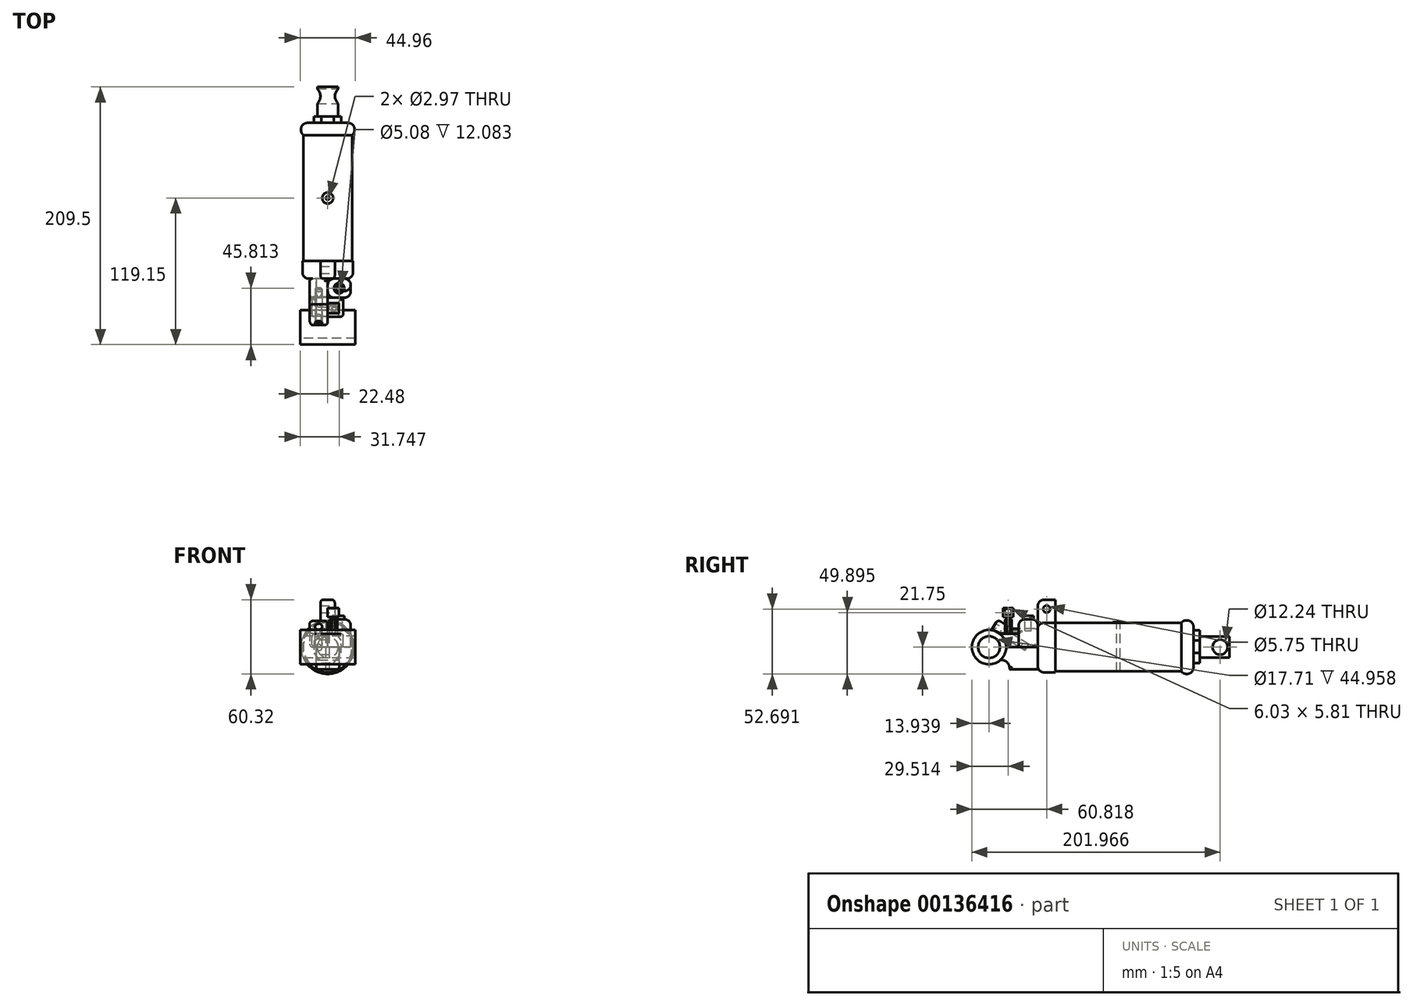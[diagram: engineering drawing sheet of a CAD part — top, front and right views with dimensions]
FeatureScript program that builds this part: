
annotation { "Feature Type Name" : "Feature", "Feature Type Description" : "" }
export const myFeature = defineFeature(function(context is Context, id is Id, definition is map)
    precondition{}
    {
        {
            var Q0;
            Q0=qCreatedBy(makeId("Front.planeOp"),FACE);
            var sketch = newSketch(context, id + "F0", { "sketchPlane" : qUnion([Q0])});
            skCircle(sketch, "E0", {"center": v(0, 0) * mm, "radius": 19.78 * mm});
            skSolve(sketch);
        }
        {
            var Q0;
            Q0=qSketchRegion(id+"F0",true);
            extrude(context, id + "F1", {"entities" : qUnion([Q0]), "endBound" : BoundingType.SYMMETRIC, "depth" : 102.44 * mm});
        }
        {
            var Q0;
            Q0=makeQuery(id+"F1.opExtrude","CAP_FACE",FACE,{"disambiguationData":[OSD([sQuery(id+"F0.wireOp",EDGE,"E0")])],"isStart":true});
            var sketch = newSketch(context, id + "F2", { "sketchPlane" : qUnion([Q0])});
            skCircle(sketch, "E1", {"center": v(0, 0) * mm, "radius": 21.75 * mm});
            skSolve(sketch);
        }
        {
            var Q0;
            Q0=qSketchRegion(id+"F2",true);
            extrude(context, id + "F3", {"entities" : qUnion([Q0]), "operationType" : NewBodyOperationType.ADD, "depth" : 9.88 * mm});
        }
        {
            var Q0;
            Q0=makeQuery(id+"F3.opExtrude","CAP_FACE",FACE,{"disambiguationData":[OSD([sQuery(id+"F2.wireOp",EDGE,"E1")])],"isStart":false});
            var sketch = newSketch(context, id + "F4", { "sketchPlane" : qUnion([Q0])});
            skLineSegment(sketch, "E2", {"start": v(-4.97, 13.58) * mm, "end": v(5.19, 13.58) * mm});
            skLineSegment(sketch, "E3", {"start": v(5.19, 13.58) * mm, "end": v(11.28, 5.45) * mm});
            skLineSegment(sketch, "E4", {"start": v(11.28, 5.45) * mm, "end": v(11.28, -4.7) * mm});
            skLineSegment(sketch, "E5", {"start": v(11.28, -4.7) * mm, "end": v(5.19, -12.84) * mm});
            skLineSegment(sketch, "E6", {"start": v(5.19, -12.84) * mm, "end": v(-4.97, -12.84) * mm});
            skLineSegment(sketch, "E7", {"start": v(-4.97, -12.84) * mm, "end": v(-11.07, -4.7) * mm});
            skLineSegment(sketch, "E8", {"start": v(-11.07, -4.7) * mm, "end": v(-11.07, 5.45) * mm});
            skLineSegment(sketch, "E9", {"start": v(-11.07, 5.45) * mm, "end": v(-4.97, 13.58) * mm});
            skSolve(sketch);
        }
        {
            var Q0;
            Q0=qSketchRegion(id+"F4",true);
            extrude(context, id + "F5", {"entities" : qUnion([Q0]), "operationType" : NewBodyOperationType.ADD, "depth" : 5.07 * mm});
        }
        {
            var Q0;
            Q0=makeQuery(id+"F5.opExtrude","CAP_FACE",FACE,{"disambiguationData":[OSD([sQuery(id+"F4.wireOp",EDGE,"E2"),sQuery(id+"F4.wireOp",EDGE,"E3"),sQuery(id+"F4.wireOp",EDGE,"E4"),sQuery(id+"F4.wireOp",EDGE,"E5"),sQuery(id+"F4.wireOp",EDGE,"E6"),sQuery(id+"F4.wireOp",EDGE,"E7"),sQuery(id+"F4.wireOp",EDGE,"E8"),sQuery(id+"F4.wireOp",EDGE,"E9")])],"isStart":false});
            var sketch = newSketch(context, id + "F6", { "sketchPlane" : qUnion([Q0])});
            skCircle(sketch, "E10", {"center": v(0, 0) * mm, "radius": 8.5 * mm});
            skSolve(sketch);
        }
        {
            var Q0;
            Q0=qSketchRegion(id+"F6",true);
            extrude(context, id + "F7", {"entities" : qUnion([Q0]), "operationType" : NewBodyOperationType.ADD, "depth" : 24.18 * mm});
        }
        {
            var Q0;
            Q0=qCreatedBy(makeId("Right.planeOp"),FACE);
            var sketch = newSketch(context, id + "F8", { "sketchPlane" : qUnion([Q0])});
            skCircle(sketch, "E11", {"center": v(82.82, 0) * mm, "radius": 6.12 * mm});
            skSolve(sketch);
        }
        {
            var Q0;
            Q0=qSketchRegion(id+"F8",true);
            extrude(context, id + "F9", {"entities" : qUnion([Q0]), "operationType" : NewBodyOperationType.REMOVE, "endBound" : BoundingType.SYMMETRIC, "oppositeDirection" : true, "depth" : 25.4 * mm});
        }
        {
            var Q0;
            Q0=qCreatedBy(makeId("Top.planeOp"),FACE);
            cPlane(context, id + "F10", {"entities" : qUnion([Q0]), "cplaneType" : CPlaneType.OFFSET, "offset" : 19.78 * mm, "width" : 152.4 * mm, "height" : 152.4 * mm});
        }
        {
            var Q0;
            Q0=qCreatedBy(id+"F10.planeOp",FACE);
            var sketch = newSketch(context, id + "F11", { "sketchPlane" : qUnion([Q0])});
            skCircle(sketch, "E12", {"center": v(0, 0) * mm, "radius": 4.5 * mm});
            skSolve(sketch);
        }
        {
            var Q0;
            Q0=qSketchRegion(id+"F11",true);
            extrude(context, id + "F12", {"entities" : qUnion([Q0]), "depth" : 0.62 * mm});
        }
        {
            var Q0;
            Q0=makeQuery(id+"F12.opExtrude","CAP_FACE",FACE,{"disambiguationData":[OSD([sQuery(id+"F11.wireOp",EDGE,"E12")])],"isStart":false});
            var sketch = newSketch(context, id + "F13", { "sketchPlane" : qUnion([Q0])});
            skCircle(sketch, "E13", {"center": v(0, 0) * mm, "radius": 1.48 * mm});
            skSolve(sketch);
        }
        {
            var Q0;
            Q0=qSketchRegion(id+"F13",true);
            extrude(context, id + "F14", {"entities" : qUnion([Q0]), "operationType" : NewBodyOperationType.REMOVE, "oppositeDirection" : true, "depth" : 152.4 * mm});
        }
        {
            var Q0;
            Q0=makeQuery(id+"F1.opExtrude","CAP_FACE",FACE,{"disambiguationData":[OSD([sQuery(id+"F0.wireOp",EDGE,"E0")])],"isStart":false});
            var sketch = newSketch(context, id + "F15", { "sketchPlane" : qUnion([Q0])});
            skCircle(sketch, "E14", {"center": v(0, 0) * mm, "radius": 20.57 * mm});
            skLineSegment(sketch, "E15", {"start": v(-5.98, 19.68) * mm, "end": v(-5.98, 38.57) * mm});
            skLineSegment(sketch, "E16", {"start": v(-5.98, 38.57) * mm, "end": v(5.75, 38.57) * mm});
            skLineSegment(sketch, "E17", {"start": v(5.75, 38.57) * mm, "end": v(5.75, 19.75) * mm});
            skSolve(sketch);
        }
        {
            var Q0;
            Q0=qSketchRegion(id+"F15",true);
            extrude(context, id + "F16", {"entities" : qUnion([Q0]), "operationType" : NewBodyOperationType.ADD, "depth" : 14.33 * mm});
        }
        {
            var Q0;
            Q0=makeQuery(id+"F16.opExtrude","CAP_EDGE",EDGE,{"disambiguationData":[OSD([sQuery(id+"F15.wireOp",EDGE,"E16")])],"isStart":false});
            fillet(context, id + "F17", {"entities" : qUnion([Q0]), "radius" : 5.08 * mm, "tangentPropagation" : true, "allowEdgeOverflow" : false});
        }
        {
            var Q0;
            Q0=makeQuery(id+"F16.opExtrude","SWEPT_EDGE",EDGE,{"disambiguationData":[OSD([sQuery(id+"F15.wireOp",EDGE,"E16"),sQuery(id+"F15.wireOp",EDGE,"E17")])]});
            var Q1;
            Q1=makeQuery(id+"F16.opExtrude","SWEPT_EDGE",EDGE,{"disambiguationData":[OSD([sQuery(id+"F15.wireOp",EDGE,"E15"),sQuery(id+"F15.wireOp",EDGE,"E16")])]});
            fillet(context, id + "F18", {"entities" : qUnion([Q0, Q1]), "radius" : 2.54 * mm, "tangentPropagation" : true, "allowEdgeOverflow" : false});
        }
        {
            var Q0;
            Q0=makeQuery(id+"F16.opExtrude","SWEPT_FACE",FACE,{"disambiguationData":[OSD([sQuery(id+"F15.wireOp",EDGE,"E17")])]});
            var sketch = newSketch(context, id + "F19", { "sketchPlane" : qUnion([Q0])});
            skCircle(sketch, "E18", {"center": v(-58.33, 30.94) * mm, "radius": 2.87 * mm});
            skSolve(sketch);
        }
        {
            var Q0;
            Q0=qSketchRegion(id+"F19",true);
            extrude(context, id + "F20", {"entities" : qUnion([Q0]), "operationType" : NewBodyOperationType.REMOVE, "endBound" : BoundingType.THROUGH_ALL, "oppositeDirection" : true, "depth" : 25.4 * mm});
        }
        {
            var Q0;
            Q0=qCreatedBy(makeId("Right.planeOp"),FACE);
            var sketch = newSketch(context, id + "F21", { "sketchPlane" : qUnion([Q0])});
            skLineSegment(sketch, "E19", {"start": v(-65.55, -17.99) * mm, "end": v(-88.58, -17.99) * mm});
            skArc(sketch, "E20", {"start": v(-88.58, -17.99) * mm, "mid": v(-90.47, -12.4) * mm, "end": v(-96.05, -10.5) * mm});
            skCircle(sketch, "E21", {"center": v(-105.21, 0) * mm, "radius": 13.94 * mm});
            skCircle(sketch, "E22", {"center": v(-105.21, 0) * mm, "radius": 8.86 * mm});
            skLineSegment(sketch, "E23", {"start": v(-96.43, 10.84) * mm, "end": v(-81.06, 10.84) * mm});
            skLineSegment(sketch, "E24", {"start": v(-81.06, 0) * mm, "end": v(-81.06, 22.72) * mm});
            skLineSegment(sketch, "E25", {"start": v(-81.06, 22.72) * mm, "end": v(-65.54, 22.72) * mm});
            skLineSegment(sketch, "E26", {"start": v(-65.54, 22.72) * mm, "end": v(-65.55, -17.99) * mm});
            skLineSegment(sketch, "E27", {"start": v(-81.06, 0) * mm, "end": v(-65.54, 0) * mm});
            skLineSegment(sketch, "E28", {"start": v(-81.06, 0) * mm, "end": v(-91.27, 0) * mm});
            skSolve(sketch);
        }
        {
            var Q0;
            {var subQ1=sQuery(id+"F21.wireOp",EDGE,"E19");Q0=makeQuery(id+"F21.imprint","IMPRINT",FACE,{"disambiguationData":[TD([[makeQuery(id+"F21.imprint","IMPRINT",EDGE,{"derivedFrom":subQ1}),-1.0]])]});}
            extrude(context, id + "F22", {"entities" : qUnion([Q0]), "endBound" : BoundingType.SYMMETRIC, "oppositeDirection" : true, "depth" : 18.93 * mm});
        }
        {
            var Q0;
            {var subQ0=sQuery(id+"F21.wireOp",EDGE,"E25");Q0=makeQuery(id+"F21.imprint","IMPRINT",FACE,{"disambiguationData":[TD([[makeQuery(id+"F21.imprint","IMPRINT",EDGE,{"derivedFrom":subQ0}),-1.0]])]});}
            extrude(context, id + "F23", {"entities" : qUnion([Q0]), "depth" : 18.67 * mm});
        }
        {
            var Q0;
            {var subQ0=sQuery(id+"F21.wireOp",EDGE,"E23");Q0=makeQuery(id+"F21.imprint","IMPRINT",FACE,{"disambiguationData":[TD([[makeQuery(id+"F21.imprint","IMPRINT",EDGE,{"derivedFrom":subQ0}),-1.0]])]});}
            extrude(context, id + "F24", {"entities" : qUnion([Q0]), "endBound" : BoundingType.SYMMETRIC, "depth" : 25.4 * mm});
        }
        {
            var Q0;
            Q0=makeQuery(id+"F21.imprint","IMPRINT",FACE,{"disambiguationData":[TD([[makeQuery(id+"F21.imprint","IMPRINT",EDGE,{"derivedFrom":sQuery(id+"F21.wireOp",EDGE,"E22")}),-1.0]])]});
            extrude(context, id + "F25", {"entities" : qUnion([Q0]), "endBound" : BoundingType.SYMMETRIC, "depth" : 44.96 * mm});
        }
        {
            var Q0;
            Q0=makeQuery(id+"F23.opExtrude","CAP_EDGE",EDGE,{"disambiguationData":[OSD([sQuery(id+"F21.wireOp",EDGE,"E25")])],"isStart":false});
            var Q1;
            Q1=makeQuery(id+"F23.opExtrude","CAP_EDGE",EDGE,{"disambiguationData":[OSD([sQuery(id+"F21.wireOp",EDGE,"E24")])],"isStart":false});
            var Q2;
            Q2=makeQuery(id+"F23.opExtrude","CAP_EDGE",EDGE,{"disambiguationData":[OSD([sQuery(id+"F21.wireOp",EDGE,"E26")])],"isStart":false});
            var Q3;
            Q3=makeQuery(id+"F23.opExtrude","SWEPT_EDGE",EDGE,{"disambiguationData":[OSD([sQuery(id+"F21.wireOp",EDGE,"E25"),sQuery(id+"F21.wireOp",EDGE,"E26")])]});
            var Q4;
            Q4=makeQuery(id+"F23.opExtrude","CAP_EDGE",EDGE,{"disambiguationData":[OSD([sQuery(id+"F21.wireOp",EDGE,"E24")])],"isStart":true});
            var Q5;
            Q5=makeQuery(id+"F23.opExtrude","CAP_EDGE",EDGE,{"disambiguationData":[OSD([sQuery(id+"F21.wireOp",EDGE,"E25")])],"isStart":true});
            fillet(context, id + "F26", {"entities" : qUnion([Q0, Q1, Q2, Q3, Q4, Q5]), "radius" : 5.08 * mm, "tangentPropagation" : true, "allowEdgeOverflow" : false});
        }
        {
            var Q0;
            Q0=makeQuery(id+"F16.opExtrude","CAP_EDGE",EDGE,{"disambiguationData":[OSD([sQuery(id+"F15.wireOp",EDGE,"E14")])],"isStart":false});
            var Q1;
            {var subQ0=sQuery(id+"F21.wireOp",EDGE,"E26");var subQ1=sQuery(id+"F21.wireOp",EDGE,"E25");Q1=makeQuery(id+"F26.opFillet","BLEND_FACE",FACE,{"disambiguationData":[OSD([subQ1,subQ0]),TDD([makeQuery(id+"F23.opExtrude","SWEPT_EDGE",EDGE,{"disambiguationData":[OSD([subQ1,subQ0])]})])]});}
            var Q2;
            Q2=makeQuery(id+"F23.opExtrude","SWEPT_EDGE",EDGE,{"disambiguationData":[OSD([sQuery(id+"F21.wireOp",EDGE,"E24"),sQuery(id+"F21.wireOp",EDGE,"E25")])]});
            fillet(context, id + "F27", {"entities" : qUnion([Q0, Q1, Q2]), "radius" : 5.08 * mm, "tangentPropagation" : true, "allowEdgeOverflow" : false});
        }
        {
            var Q0;
            Q0=makeQuery(id+"F23.opExtrude","SWEPT_FACE",FACE,{"disambiguationData":[OSD([sQuery(id+"F21.wireOp",EDGE,"E25")])]});
            var sketch = newSketch(context, id + "F28", { "sketchPlane" : qUnion([Q0])});
            skPoint(sketch, "E29.centerSnap0", {"position": v(9.34, -75.98) * mm});
            skCircle(sketch, "E30", {"center": v(9.27, -73.34) * mm, "radius": 4.22 * mm});
            skSolve(sketch);
        }
        {
            var Q0;
            Q0=qSketchRegion(id+"F28",true);
            extrude(context, id + "F29", {"entities" : qUnion([Q0]), "operationType" : NewBodyOperationType.ADD, "depth" : 2.35 * mm});
        }
        {
            var Q0;
            Q0=qSketchRegion(id+"F28",true);
            extrude(context, id + "F30", {"entities" : qUnion([Q0]), "operationType" : NewBodyOperationType.ADD, "depth" : 2.86 * mm});
        }
        {
            var Q0;
            Q0=makeQuery(id+"F30.opExtrude","CAP_FACE",FACE,{"disambiguationData":[OSD([sQuery(id+"F28.wireOp",EDGE,"E30")])],"isStart":false});
            var sketch = newSketch(context, id + "F31", { "sketchPlane" : qUnion([Q0])});
            skCircle(sketch, "E31", {"center": v(9.27, -73.34) * mm, "radius": 2.54 * mm});
            skSolve(sketch);
        }
        {
            var Q0;
            Q0=qSketchRegion(id+"F31",true);
            extrude(context, id + "F32", {"entities" : qUnion([Q0]), "operationType" : NewBodyOperationType.REMOVE, "oppositeDirection" : true, "depth" : 12.08 * mm});
        }
        {
            var Q0;
            Q0=makeQuery(id+"F24.opExtrude","CAP_EDGE",EDGE,{"disambiguationData":[OSD([sQuery(id+"F21.wireOp",EDGE,"E23")])],"isStart":false});
            var Q1;
            Q1=makeQuery(id+"F24.opExtrude","CAP_EDGE",EDGE,{"disambiguationData":[OSD([sQuery(id+"F21.wireOp",EDGE,"E23")])],"isStart":true});
            var Q2;
            Q2=makeQuery(id+"F24.opExtrude","SWEPT_EDGE",EDGE,{"disambiguationData":[OSD([sQuery(id+"F21.wireOp",EDGE,"E23"),sQuery(id+"F21.wireOp",EDGE,"E24")])]});
            var Q3;
            Q3=makeQuery(id+"F22.opExtrude","CAP_EDGE",EDGE,{"disambiguationData":[OSD([sQuery(id+"F21.wireOp",EDGE,"E27"),sQuery(id+"F21.wireOp",EDGE,"E28")])],"isStart":false});
            var Q4;
            Q4=makeQuery(id+"F22.opExtrude","CAP_EDGE",EDGE,{"disambiguationData":[OSD([sQuery(id+"F21.wireOp",EDGE,"E19")])],"isStart":true});
            var Q5;
            Q5=makeQuery(id+"F22.opExtrude","CAP_EDGE",EDGE,{"disambiguationData":[OSD([sQuery(id+"F21.wireOp",EDGE,"E20")])],"isStart":true});
            var Q6;
            Q6=makeQuery(id+"F24.opExtrude","CAP_EDGE",EDGE,{"disambiguationData":[OSD([sQuery(id+"F21.wireOp",EDGE,"E28")])],"isStart":false});
            fillet(context, id + "F33", {"entities" : qUnion([Q0, Q1, Q2, Q3, Q4, Q5, Q6]), "radius" : 2.03 * mm, "tangentPropagation" : true, "allowEdgeOverflow" : false});
        }
        {
            var Q0;
            Q0=makeQuery(id+"F22.opExtrude","CAP_EDGE",EDGE,{"disambiguationData":[OSD([sQuery(id+"F21.wireOp",EDGE,"E19")])],"isStart":false});
            var Q1;
            Q1=makeQuery(id+"F22.opExtrude","CAP_EDGE",EDGE,{"disambiguationData":[OSD([sQuery(id+"F21.wireOp",EDGE,"E20")])],"isStart":false});
            var Q2;
            Q2=makeQuery(id+"F24.opExtrude","CAP_EDGE",EDGE,{"disambiguationData":[OSD([sQuery(id+"F21.wireOp",EDGE,"E28")])],"isStart":true});
            fillet(context, id + "F34", {"entities" : qUnion([Q0, Q1, Q2]), "radius" : 2.03 * mm, "tangentPropagation" : true, "allowEdgeOverflow" : false});
        }
        {
            var Q0;
            {var subQ0=sQuery(id+"F21.wireOp",EDGE,"E25");Q0=makeQuery(id+"F21.imprint","IMPRINT",FACE,{"disambiguationData":[TD([[makeQuery(id+"F21.imprint","IMPRINT",EDGE,{"derivedFrom":subQ0}),-1.0]])]});}
            var sketch = newSketch(context, id + "F35", { "sketchPlane" : qUnion([Q0])});
            skLineSegment(sketch, "E32", {"start": v(-65.36, 14.9) * mm, "end": v(-86.46, 14.9) * mm});
            skLineSegment(sketch, "E33", {"start": v(-86.46, 14.9) * mm, "end": v(-98.1, 22.23) * mm});
            skLineSegment(sketch, "E34", {"start": v(-98.1, 22.23) * mm, "end": v(-103.37, 13.85) * mm});
            skArc(sketch, "E35", {"start": v(-91.2, 0) * mm, "mid": v(-94.44, 9.43) * mm, "end": v(-103.37, 13.85) * mm});
            skLineSegment(sketch, "E36", {"start": v(-65.36, 14.9) * mm, "end": v(-65.36, 0) * mm});
            skLineSegment(sketch, "E37", {"start": v(-65.36, 0) * mm, "end": v(-80.43, 0) * mm});
            skLineSegment(sketch, "E38", {"start": v(-80.43, 0) * mm, "end": v(-80.43, 11.03) * mm});
            skLineSegment(sketch, "E39", {"start": v(-80.43, 11.03) * mm, "end": v(-96.13, 11.03) * mm});
            skSolve(sketch);
        }
        {
            var Q0;
            Q0=qSketchRegion(id+"F35",true);
            extrude(context, id + "F36", {"entities" : qUnion([Q0]), "oppositeDirection" : true, "depth" : 14.7 * mm});
        }
        {
            var Q0;
            Q0=makeQuery(id+"F36.opExtrude","CAP_EDGE",EDGE,{"disambiguationData":[OSD([sQuery(id+"F35.wireOp",EDGE,"E37")])],"isStart":false});
            var Q1;
            Q1=makeQuery(id+"F36.opExtrude","CAP_EDGE",EDGE,{"disambiguationData":[OSD([sQuery(id+"F35.wireOp",EDGE,"E38")])],"isStart":false});
            var Q2;
            Q2=makeQuery(id+"F36.opExtrude","CAP_EDGE",EDGE,{"disambiguationData":[OSD([sQuery(id+"F35.wireOp",EDGE,"E39")])],"isStart":false});
            var Q3;
            Q3=makeQuery(id+"F36.opExtrude","CAP_EDGE",EDGE,{"disambiguationData":[OSD([sQuery(id+"F35.wireOp",EDGE,"E35")])],"isStart":false});
            var Q4;
            Q4=makeQuery(id+"F36.opExtrude","CAP_EDGE",EDGE,{"disambiguationData":[OSD([sQuery(id+"F35.wireOp",EDGE,"E34")])],"isStart":false});
            var Q5;
            Q5=makeQuery(id+"F36.opExtrude","CAP_EDGE",EDGE,{"disambiguationData":[OSD([sQuery(id+"F35.wireOp",EDGE,"E33")])],"isStart":false});
            var Q6;
            Q6=makeQuery(id+"F36.opExtrude","SWEPT_EDGE",EDGE,{"disambiguationData":[OSD([sQuery(id+"F35.wireOp",EDGE,"E33"),sQuery(id+"F35.wireOp",EDGE,"E34")])]});
            var Q7;
            Q7=makeQuery(id+"F36.opExtrude","CAP_EDGE",EDGE,{"disambiguationData":[OSD([sQuery(id+"F35.wireOp",EDGE,"E32")])],"isStart":false});
            var Q8;
            Q8=makeQuery(id+"F36.opExtrude","CAP_EDGE",EDGE,{"disambiguationData":[OSD([sQuery(id+"F35.wireOp",EDGE,"E32")])],"isStart":true});
            var Q9;
            Q9=makeQuery(id+"F36.opExtrude","SWEPT_EDGE",EDGE,{"disambiguationData":[OSD([sQuery(id+"F35.wireOp",EDGE,"E32"),sQuery(id+"F35.wireOp",EDGE,"E36")])]});
            var Q10;
            Q10=makeQuery(id+"F36.opExtrude","CAP_EDGE",EDGE,{"disambiguationData":[OSD([sQuery(id+"F35.wireOp",EDGE,"E36")])],"isStart":false});
            var Q11;
            Q11=makeQuery(id+"F36.opExtrude","CAP_EDGE",EDGE,{"disambiguationData":[OSD([sQuery(id+"F35.wireOp",EDGE,"E34")])],"isStart":true});
            var Q12;
            Q12=makeQuery(id+"F36.opExtrude","CAP_EDGE",EDGE,{"disambiguationData":[OSD([sQuery(id+"F35.wireOp",EDGE,"E33")])],"isStart":true});
            fillet(context, id + "F37", {"entities" : qUnion([Q0, Q1, Q2, Q3, Q4, Q5, Q6, Q7, Q8, Q9, Q10, Q11, Q12]), "radius" : 2.54 * mm, "tangentPropagation" : true, "allowEdgeOverflow" : false});
        }
        {
            var Q0;
            Q0=makeQuery(id+"F36.opExtrude","SWEPT_FACE",FACE,{"disambiguationData":[OSD([sQuery(id+"F35.wireOp",EDGE,"E34")])]});
            var sketch = newSketch(context, id + "F38", { "sketchPlane" : qUnion([Q0])});
            skCircle(sketch, "E40", {"center": v(-7.46, -39.97) * mm, "radius": 2.94 * mm});
            skSolve(sketch);
        }
        {
            var Q0;
            Q0=qSketchRegion(id+"F38",true);
            extrude(context, id + "F39", {"entities" : qUnion([Q0]), "operationType" : NewBodyOperationType.REMOVE, "oppositeDirection" : true, "depth" : 31.94 * mm});
        }
        {
            var Q0;
            Q0=makeQuery(id+"F24.opExtrude","SWEPT_FACE",FACE,{"disambiguationData":[OSD([sQuery(id+"F21.wireOp",EDGE,"E23")])]});
            var sketch = newSketch(context, id + "F40", { "sketchPlane" : qUnion([Q0])});
            skLineSegment(sketch, "E41", {"start": v(1.56, -90.61) * mm, "end": v(1.56, -88.2) * mm});
            skLineSegment(sketch, "E42", {"start": v(1.56, -88.2) * mm, "end": v(3.5, -86.74) * mm});
            skLineSegment(sketch, "E43", {"start": v(3.5, -86.74) * mm, "end": v(5.91, -86.74) * mm});
            skLineSegment(sketch, "E44", {"start": v(5.91, -86.74) * mm, "end": v(7.85, -88.2) * mm});
            skLineSegment(sketch, "E45", {"start": v(7.85, -88.2) * mm, "end": v(7.85, -90.61) * mm});
            skLineSegment(sketch, "E46", {"start": v(7.85, -90.61) * mm, "end": v(5.91, -92.06) * mm});
            skLineSegment(sketch, "E47", {"start": v(5.91, -92.06) * mm, "end": v(3.5, -92.06) * mm});
            skLineSegment(sketch, "E48", {"start": v(3.5, -92.06) * mm, "end": v(1.56, -90.61) * mm});
            skSolve(sketch);
        }
        {
            var Q0;
            Q0=qSketchRegion(id+"F40",true);
            extrude(context, id + "F41", {"entities" : qUnion([Q0]), "operationType" : NewBodyOperationType.ADD, "depth" : 11.9 * mm});
        }
        {
            var Q0;
            Q0=makeQuery(id+"F41.opExtrude","CAP_FACE",FACE,{"disambiguationData":[OSD([sQuery(id+"F40.wireOp",EDGE,"E41"),sQuery(id+"F40.wireOp",EDGE,"E42"),sQuery(id+"F40.wireOp",EDGE,"E43"),sQuery(id+"F40.wireOp",EDGE,"E44"),sQuery(id+"F40.wireOp",EDGE,"E45"),sQuery(id+"F40.wireOp",EDGE,"E46"),sQuery(id+"F40.wireOp",EDGE,"E47"),sQuery(id+"F40.wireOp",EDGE,"E48")])],"isStart":false});
            var sketch = newSketch(context, id + "F42", { "sketchPlane" : qUnion([Q0])});
            skCircle(sketch, "E49", {"center": v(4.6, -89.64) * mm, "radius": 1.5 * mm});
            skSolve(sketch);
        }
        {
            var Q0;
            Q0=makeQuery(id+"F42.imprint","IMPRINT",FACE,{"disambiguationData":[TD([[makeQuery(id+"F42.imprint","IMPRINT",EDGE,{"derivedFrom":sQuery(id+"F42.wireOp",EDGE,"E49")}),1.0]])]});
            extrude(context, id + "F43", {"entities" : qUnion([Q0]), "operationType" : NewBodyOperationType.ADD, "depth" : 1.68 * mm});
        }
        {
            var Q0;
            Q0=makeQuery(id+"F43.opExtrude","CAP_FACE",FACE,{"disambiguationData":[OSD([sQuery(id+"F42.wireOp",EDGE,"E49")])],"isStart":false});
            var sketch = newSketch(context, id + "F44", { "sketchPlane" : qUnion([Q0])});
            skLineSegment(sketch, "E50.bottom", {"start": v(9.2, -85.54) * mm, "end": v(0, -85.54) * mm});
            skLineSegment(sketch, "E50.top", {"start": v(9.2, -93.73) * mm, "end": v(0, -93.73) * mm});
            skLineSegment(sketch, "E50.left", {"start": v(9.2, -85.54) * mm, "end": v(9.2, -93.73) * mm});
            skLineSegment(sketch, "E50.right", {"start": v(0, -85.54) * mm, "end": v(0, -93.73) * mm});
            skPoint(sketch, "E50.middle", {"position": v(4.6, -89.64) * mm});
            skSolve(sketch);
        }
        {
            var Q0;
            Q0=qSketchRegion(id+"F44",true);
            extrude(context, id + "F45", {"entities" : qUnion([Q0]), "operationType" : NewBodyOperationType.ADD, "depth" : 7.47 * mm});
        }
        {
            var Q0;
            Q0=makeQuery(id+"F45.opExtrude","SWEPT_FACE",FACE,{"disambiguationData":[OSD([sQuery(id+"F44.wireOp",EDGE,"E50.left")])]});
            var sketch = newSketch(context, id + "F46", { "sketchPlane" : qUnion([Q0])});
            skLineSegment(sketch, "E51", {"start": v(-92.65, 31.05) * mm, "end": v(-92.65, 25.24) * mm});
            skLineSegment(sketch, "E52", {"start": v(-92.65, 25.24) * mm, "end": v(-86.62, 25.24) * mm});
            skLineSegment(sketch, "E53", {"start": v(-86.62, 25.24) * mm, "end": v(-86.62, 31.05) * mm});
            skLineSegment(sketch, "E54", {"start": v(-86.62, 31.05) * mm, "end": v(-92.65, 31.05) * mm});
            skSolve(sketch);
        }
        {
            var Q0;
            Q0=qSketchRegion(id+"F46",true);
            extrude(context, id + "F47", {"entities" : qUnion([Q0]), "operationType" : NewBodyOperationType.REMOVE, "endBound" : BoundingType.THROUGH_ALL, "oppositeDirection" : true, "depth" : 25.4 * mm});
        }
        {
            var Q0;
            Q0=makeQuery(id+"F47.boolean.opBoolean","COPY",FACE,{"derivedFrom":makeQuery(id+"F47.opExtrude","SWEPT_FACE",FACE,{"disambiguationData":[OSD([sQuery(id+"F46.wireOp",EDGE,"E52")])]})});
            var sketch = newSketch(context, id + "F48", { "sketchPlane" : qUnion([Q0])});
            skCircle(sketch, "E55", {"center": v(5.3, -89.74) * mm, "radius": 1.78 * mm});
            skSolve(sketch);
        }
        {
            var Q0;
            Q0=qSketchRegion(id+"F48",true);
            extrude(context, id + "F49", {"entities" : qUnion([Q0]), "operationType" : NewBodyOperationType.ADD, "depth" : 0.82 * mm});
        }
        {
            var Q0;
            Q0=makeQuery(id+"F3.opExtrude","CAP_EDGE",EDGE,{"disambiguationData":[OSD([sQuery(id+"F2.wireOp",EDGE,"E1")])],"isStart":true});
            var Q1;
            Q1=makeQuery(id+"F3.opExtrude","CAP_EDGE",EDGE,{"disambiguationData":[OSD([sQuery(id+"F2.wireOp",EDGE,"E1")])],"isStart":false});
            fillet(context, id + "F50", {"entities" : qUnion([Q0, Q1]), "radius" : 5.08 * mm, "tangentPropagation" : true, "allowEdgeOverflow" : false});
        }
    });
